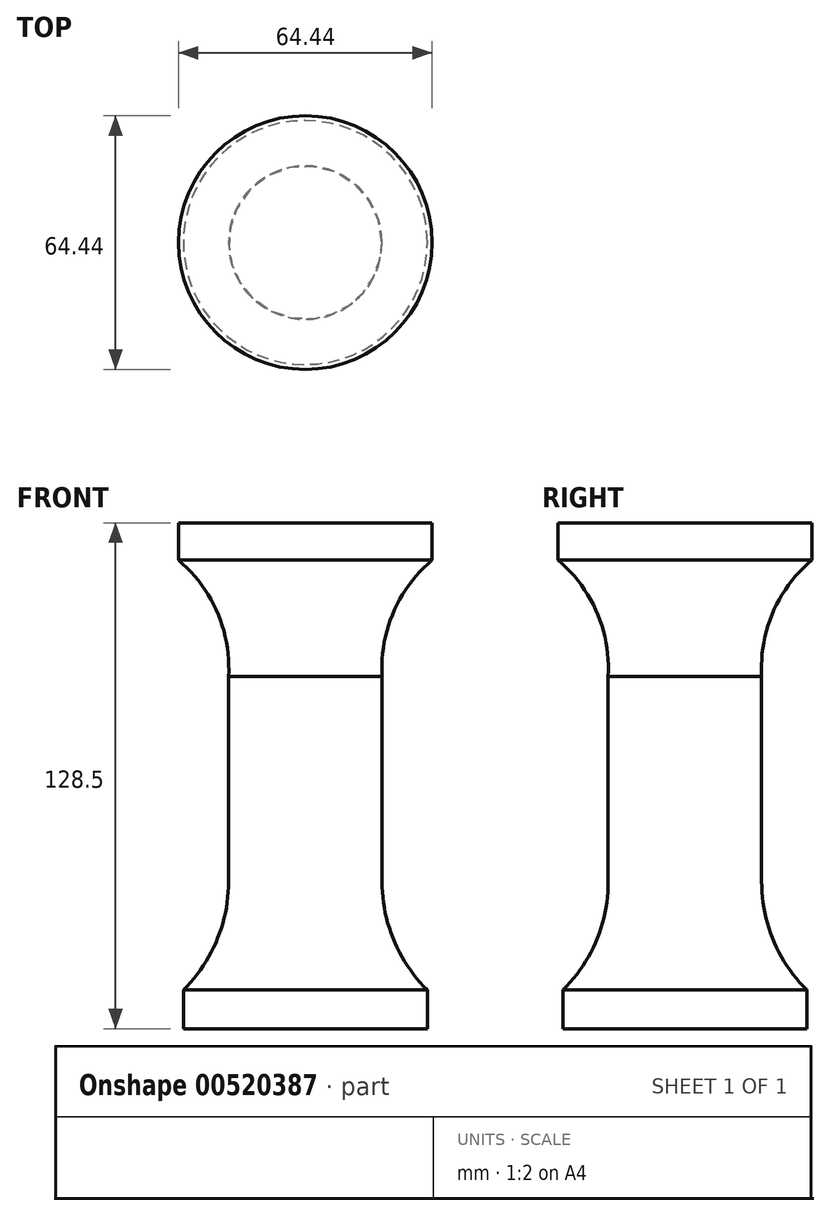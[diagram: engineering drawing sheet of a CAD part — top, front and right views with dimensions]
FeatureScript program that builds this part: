
annotation { "Feature Type Name" : "Feature", "Feature Type Description" : "" }
export const myFeature = defineFeature(function(context is Context, id is Id, definition is map)
    precondition{}
    {
        {
            var Q0;
            Q0=qCreatedBy(makeId("Front.planeOp"),FACE);
            var sketch = newSketch(context, id + "F0", { "sketchPlane" : qUnion([Q0])});
            skLineSegment(sketch, "E0", {"start": v(0, 101.96) * mm, "end": v(0, -102.5) * mm, "construction": true});
            skLineSegment(sketch, "E1", {"start": v(0, 72.81) * mm, "end": v(32.22, 72.81) * mm});
            skLineSegment(sketch, "E2", {"start": v(32.22, 72.81) * mm, "end": v(32.22, 63.37) * mm});
            skArc(sketch, "E3", {"start": v(32.22, 63.37) * mm, "mid": v(22.37, 50.09) * mm, "end": v(19.49, 33.8) * mm});
            skLineSegment(sketch, "E4", {"start": v(19.49, 33.8) * mm, "end": v(19.49, -18.33) * mm});
            skArc(sketch, "E5", {"start": v(19.49, -18.33) * mm, "mid": v(22.48, -33.24) * mm, "end": v(30.98, -45.84) * mm});
            skLineSegment(sketch, "E6", {"start": v(30.98, -45.84) * mm, "end": v(30.98, -55.7) * mm});
            skLineSegment(sketch, "E7", {"start": v(30.98, -55.7) * mm, "end": v(0, -55.7) * mm});
            skLineSegment(sketch, "E8", {"start": v(0, -55.7) * mm, "end": v(0, 72.81) * mm});
            skSolve(sketch);
        }
        {
            var Q0;
            Q0=makeQuery(id+"F0.imprint","IMPRINT",FACE,{"disambiguationData":[TD([[makeQuery(id+"F0.imprint","IMPRINT",EDGE,{"derivedFrom":sQuery(id+"F0.wireOp",EDGE,"E1")}),-1.0]])]});
            var Q1;
            Q1=sQuery(id+"F0.wireOp",EDGE,"E0");
            revolve(context, id + "F1", {"entities" : qUnion([Q0]), "axis" : qUnion([Q1]), "revolveType" : RevolveType.FULL});
        }
    });
